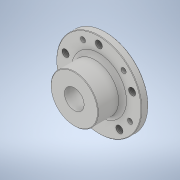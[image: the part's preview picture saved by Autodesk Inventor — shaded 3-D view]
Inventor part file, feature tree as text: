
AUTODESK INVENTOR PART (.ipt)
format: ipt  version: 2021 (Build 250183000, 183)  size: 214,528 bytes
history: native  units: in
note: dims shown in document units (in); Inventor stores cm internally (conversion verified against a paired STEP export)
features: thread x6, sketch x6, extrude x5, fillet x2, revolve x1, chamfer x1
ambient origin geometry x8: Origin, YZ Plane, XZ Plane, XY Plane, X Axis, Y Axis, Z Axis, Center Point
bodies: Solid1 (feature_tree)
feature tree (21):
  revolve  "Revolution1"  [1 undecoded]
  extrude  "Extrusion1"  Depth=0.435in
  extrude  "Extrusion2"  Depth=0.2in
  fillet  "Fillet1"  Radius=0.16in
  chamfer  "Chamfer1"  Distance=1.0in
  fillet  "Fillet2"  Radius=1.25in
  extrude  "Extrusion3"  Depth=0.435in TaperAngle=0.0deg
  thread  "Thread1"  [1 undecoded]
  thread  "Thread2"  [1 undecoded]
  thread  "Thread3"  [1 undecoded]
  thread  "Thread4"  [1 undecoded]
  thread  "Thread5"  [1 undecoded]
  thread  "Thread6"  [1 undecoded]
  extrude  "Extrusion4"  TaperAngle=45.0deg  [1 undecoded]
  extrude  "Extrusion5"  Depth=0.435in
  sketch  "Sketch1"  dims[d0=1.5in d1=1.56in]
  sketch  "Sketch2"  dims[d2=1.2in d3=0.435in]
  sketch  "Sketch3"  dims[d4=1.42in d5=0.2in d6=0.16in]
  sketch  "Sketch4"  dims[d7=0.52in]
  sketch  "Sketch5"  dims[d8=90.0deg]
  sketch  "Sketch6"  dims[d9=2.0in d10=1.0in d11=0.0in d12=1.25in d13=1.0in d14=0.0in d15=0.075in d16=0.03in d17=0.125in d18=45.0deg d19=0.25in d20=0.452in d21=0.48in d22=1.9685in d24=360.0deg d26=45.0deg d27=0.2in d28=0.2in d29=0.0in d30=0.435in d31=0.0in d32=0.435in d33=0.0in d34=0.435in d35=0.0in d36=0.435in d37=0.0in d38=0.435in d39=0.0in d40=0.435in d41=0.0in d42=1.0in d43=0.0in d44=0.325in d45=1.9685in d47=360.0deg d49=1.0in d50=0.0in]
note: 8 required parameter values undecoded (feature->parameter linkage not recoverable at this tier; creation-order binding heuristic only, values carry confidence <= 0.55)